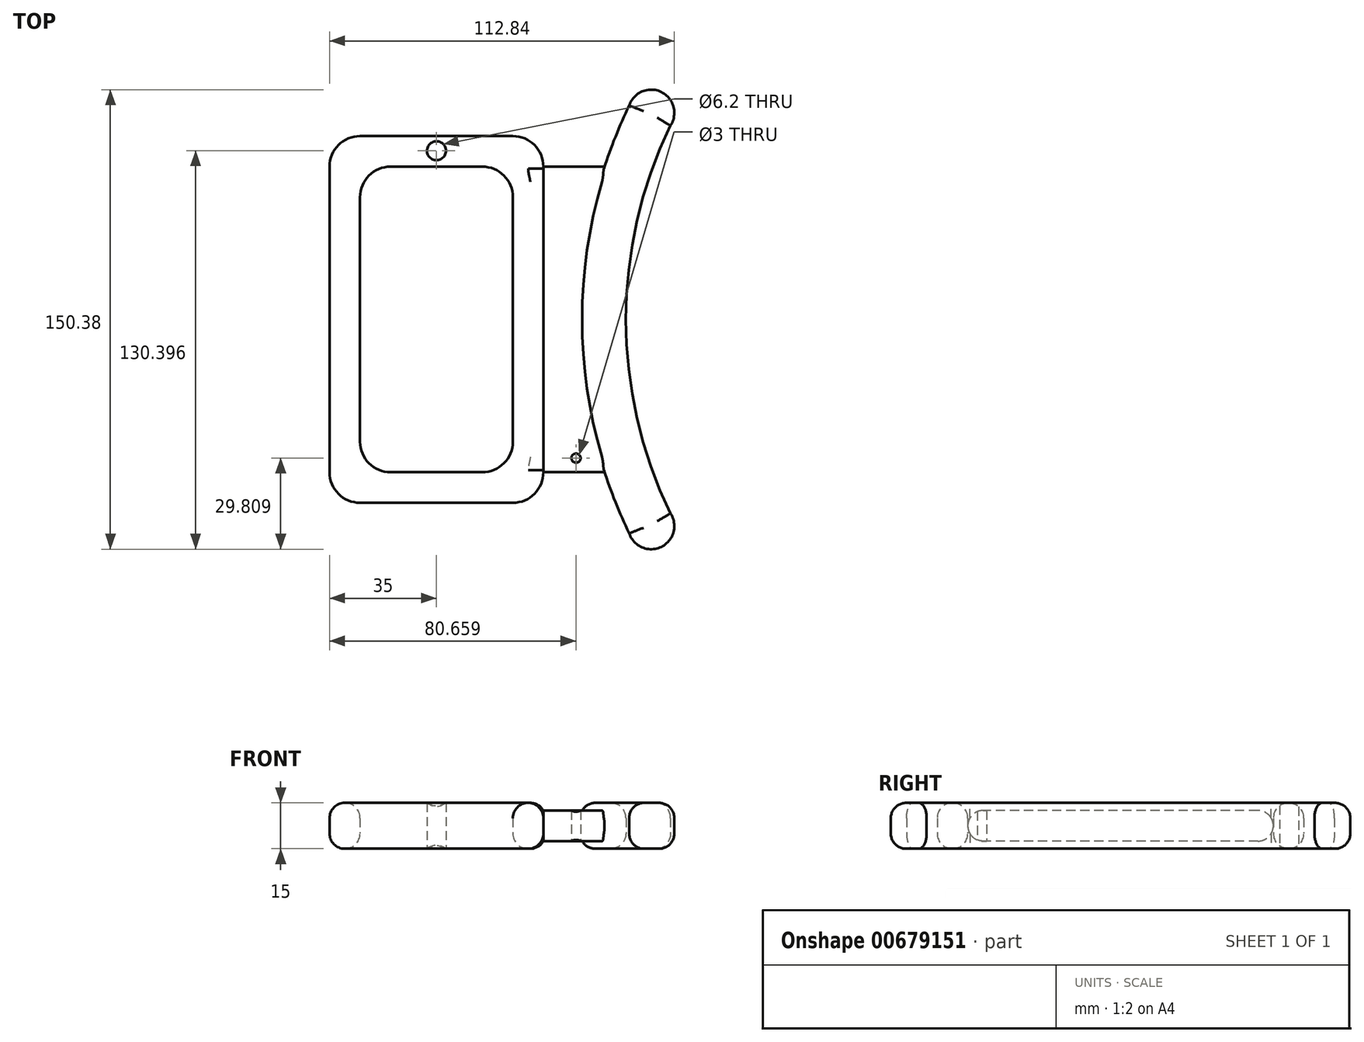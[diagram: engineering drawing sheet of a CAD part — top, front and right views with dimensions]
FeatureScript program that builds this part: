
annotation { "Feature Type Name" : "Feature", "Feature Type Description" : "" }
export const myFeature = defineFeature(function(context is Context, id is Id, definition is map)
    precondition{}
    {
        {
            var Q0;
            Q0=qCreatedBy(makeId("Top.planeOp"),FACE);
            var sketch = newSketch(context, id + "F0", { "sketchPlane" : qUnion([Q0])});
            skLineSegment(sketch, "E0.bottom", {"start": v(15, 50) * mm, "end": v(-15, 50) * mm});
            skLineSegment(sketch, "E0.top", {"start": v(15, -50) * mm, "end": v(-15, -50) * mm});
            skLineSegment(sketch, "E0.left", {"start": v(25, 40) * mm, "end": v(25, -40) * mm});
            skLineSegment(sketch, "E0.right", {"start": v(-25, 40) * mm, "end": v(-25, -40) * mm});
            skPoint(sketch, "E0.middle", {"position": v(0, 0) * mm});
            skLineSegment(sketch, "E1.0", {"start": v(35, 50) * mm, "end": v(35, -50) * mm});
            skLineSegment(sketch, "E1.1", {"start": v(25, 60) * mm, "end": v(-25, 60) * mm});
            skLineSegment(sketch, "E1.2", {"start": v(-35, 50) * mm, "end": v(-35, -50) * mm});
            skLineSegment(sketch, "E1.3", {"start": v(25, -60) * mm, "end": v(-25, -60) * mm});
            skLineSegment(sketch, "E2", {"start": v(35, -50) * mm, "end": v(55, -50) * mm});
            skLineSegment(sketch, "E3", {"start": v(0, 0) * mm, "end": v(75.3, 0) * mm, "construction": true});
            skLineSegment(sketch, "E4.MirrorCS", {"start": v(35, 50) * mm, "end": v(55, 50) * mm});
            skArc(sketch, "E5", {"start": v(63.1, 70) * mm, "mid": v(47, 0) * mm, "end": v(63.1, -70) * mm});
            skLineSegment(sketch, "E6.0", {"start": v(0, -70) * mm, "end": v(75.3, -70) * mm, "construction": true});
            skArc(sketch, "E7.0", {"start": v(76.59, 63.45) * mm, "mid": v(62, 0) * mm, "end": v(76.59, -63.45) * mm});
            skArc(sketch, "E8", {"start": v(76.59, 63.45) * mm, "mid": v(73.58, 74.43) * mm, "end": v(63.1, 70) * mm});
            skArc(sketch, "E9.MirrorCS", {"start": v(76.59, -63.45) * mm, "mid": v(73.58, -74.43) * mm, "end": v(63.1, -70) * mm});
            skPoint(sketch, "E10.visualSharp", {"position": v(-35, 60) * mm});
            skArc(sketch, "E10.filletArc", {"start": v(-25, 60) * mm, "mid": v(-32.07, 57.07) * mm, "end": v(-35, 50) * mm});
            skPoint(sketch, "E11.visualSharp", {"position": v(-35, -60) * mm});
            skArc(sketch, "E11.filletArc", {"start": v(-35, -50) * mm, "mid": v(-32.07, -57.07) * mm, "end": v(-25, -60) * mm});
            skPoint(sketch, "E12.visualSharp", {"position": v(35, 60) * mm});
            skArc(sketch, "E12.filletArc", {"start": v(35, 50) * mm, "mid": v(32.07, 57.07) * mm, "end": v(25, 60) * mm});
            skPoint(sketch, "E13.visualSharp", {"position": v(35, -60) * mm});
            skArc(sketch, "E13.filletArc", {"start": v(25, -60) * mm, "mid": v(32.07, -57.07) * mm, "end": v(35, -50) * mm});
            skArc(sketch, "E14.filletArc", {"start": v(25, 40) * mm, "mid": v(22.07, 47.07) * mm, "end": v(15, 50) * mm});
            skArc(sketch, "E15.filletArc", {"start": v(-15, 50) * mm, "mid": v(-22.07, 47.07) * mm, "end": v(-25, 40) * mm});
            skArc(sketch, "E16.filletArc", {"start": v(-25, -40) * mm, "mid": v(-22.07, -47.07) * mm, "end": v(-15, -50) * mm});
            skArc(sketch, "E17.filletArc", {"start": v(15, -50) * mm, "mid": v(22.07, -47.07) * mm, "end": v(25, -40) * mm});
            skCircle(sketch, "E18", {"center": v(0, 55.2) * mm, "radius": 3.1 * mm});
            skCircle(sketch, "E19", {"center": v(45.66, -45.38) * mm, "radius": 1.5 * mm});
            skSolve(sketch);
        }
        {
            var Q0;
            Q0=makeQuery(id+"F0.imprint","IMPRINT",FACE,{"disambiguationData":[TD([[makeQuery(id+"F0.imprint","IMPRINT",EDGE,{"derivedFrom":sQuery(id+"F0.wireOp",EDGE,"E0.bottom")}),-1.0]])]});
            extrude(context, id + "F1", {"entities" : qUnion([Q0]), "endBound" : BoundingType.SYMMETRIC, "depth" : 15 * mm, "offsetDistance" : 25 * mm});
        }
        {
            var Q0;
            Q0=makeQuery(id+"F0.imprint","IMPRINT",FACE,{"disambiguationData":[TD([[makeQuery(id+"F0.imprint","IMPRINT",EDGE,{"derivedFrom":sQuery(id+"F0.wireOp",EDGE,"E1.0")}),1.0]])]});
            extrude(context, id + "F2", {"entities" : qUnion([Q0]), "operationType" : NewBodyOperationType.ADD, "endBound" : BoundingType.SYMMETRIC, "depth" : 10 * mm, "offsetDistance" : 25 * mm});
        }
        {
            var Q0;
            Q0=makeQuery(id+"F0.imprint","IMPRINT",FACE,{"disambiguationData":[TD([[makeQuery(id+"F0.imprint","IMPRINT",EDGE,{"derivedFrom":sQuery(id+"F0.wireOp",EDGE,"E7.0")}),-1.0]])]});
            extrude(context, id + "F3", {"entities" : qUnion([Q0]), "operationType" : NewBodyOperationType.ADD, "endBound" : BoundingType.SYMMETRIC, "depth" : 15 * mm, "offsetDistance" : 25 * mm});
        }
        {
            var Q0;
            Q0=makeQuery(id+"F1.opExtrude","CAP_EDGE",EDGE,{"disambiguationData":[OSD([sQuery(id+"F0.wireOp",EDGE,"E0.left")])],"isStart":true});
            fillet(context, id + "F4", {"entities" : qUnion([Q0]), "radius" : 5 * mm, "tangentPropagation" : true, "allowEdgeOverflow" : false});
        }
        {
            var Q0;
            Q0=makeQuery(id+"F1.opExtrude","CAP_EDGE",EDGE,{"disambiguationData":[OSD([sQuery(id+"F0.wireOp",EDGE,"E0.right")])],"isStart":false});
            fillet(context, id + "F5", {"entities" : qUnion([Q0]), "radius" : 5 * mm, "tangentPropagation" : true, "allowEdgeOverflow" : false});
        }
        {
            var Q0;
            Q0=makeQuery(id+"F3.opExtrude","CAP_EDGE",EDGE,{"disambiguationData":[OSD([sQuery(id+"F0.wireOp",EDGE,"E5")])],"isStart":true});
            var Q1;
            Q1=makeQuery(id+"F3.opExtrude","CAP_EDGE",EDGE,{"disambiguationData":[OSD([sQuery(id+"F0.wireOp",EDGE,"E5")])],"isStart":false});
            var Q2;
            Q2=makeQuery(id+"F3.opExtrude","CAP_EDGE",EDGE,{"disambiguationData":[OSD([sQuery(id+"F0.wireOp",EDGE,"E7.0")])],"isStart":false});
            var Q3;
            Q3=makeQuery(id+"F3.opExtrude","CAP_EDGE",EDGE,{"disambiguationData":[OSD([sQuery(id+"F0.wireOp",EDGE,"E7.0")])],"isStart":true});
            var Q4;
            Q4=makeQuery(id+"F3.opExtrude","CAP_EDGE",EDGE,{"disambiguationData":[OSD([sQuery(id+"F0.wireOp",EDGE,"E8")])],"isStart":false});
            var Q5;
            Q5=makeQuery(id+"F3.opExtrude","CAP_EDGE",EDGE,{"disambiguationData":[OSD([sQuery(id+"F0.wireOp",EDGE,"E9.MirrorCS")])],"isStart":false});
            var Q6;
            Q6=makeQuery(id+"F3.opExtrude","CAP_EDGE",EDGE,{"disambiguationData":[OSD([sQuery(id+"F0.wireOp",EDGE,"E8")])],"isStart":true});
            var Q7;
            Q7=makeQuery(id+"F3.opExtrude","CAP_EDGE",EDGE,{"disambiguationData":[OSD([sQuery(id+"F0.wireOp",EDGE,"E9.MirrorCS")])],"isStart":true});
            fillet(context, id + "F6", {"entities" : qUnion([Q0, Q1, Q2, Q3, Q4, Q5, Q6, Q7]), "radius" : 5 * mm, "tangentPropagation" : true, "allowEdgeOverflow" : false});
        }
        {
            var Q0;
            Q0=makeQuery(id+"F2.opExtrude","CAP_EDGE",EDGE,{"disambiguationData":[OSD([sQuery(id+"F0.wireOp",EDGE,"E4.MirrorCS")])],"isStart":true});
            var Q1;
            Q1=makeQuery(id+"F2.opExtrude","CAP_EDGE",EDGE,{"disambiguationData":[OSD([sQuery(id+"F0.wireOp",EDGE,"E2")])],"isStart":true});
            var Q2;
            Q2=makeQuery(id+"F2.opExtrude","CAP_EDGE",EDGE,{"disambiguationData":[OSD([sQuery(id+"F0.wireOp",EDGE,"E2")])],"isStart":false});
            var Q3;
            Q3=makeQuery(id+"F2.opExtrude","CAP_EDGE",EDGE,{"disambiguationData":[OSD([sQuery(id+"F0.wireOp",EDGE,"E4.MirrorCS")])],"isStart":false});
            fillet(context, id + "F7", {"entities" : qUnion([Q0, Q1, Q2, Q3]), "radius" : 5 * mm, "tangentPropagation" : true, "allowEdgeOverflow" : false});
        }
        {
            var Q0;
            Q0=makeQuery(id+"F1.opExtrude","CAP_EDGE",EDGE,{"disambiguationData":[OSD([sQuery(id+"F0.wireOp",EDGE,"E1.2")])],"isStart":true});
            var Q1;
            Q1=makeQuery(id+"F1.opExtrude","CAP_EDGE",EDGE,{"disambiguationData":[OSD([sQuery(id+"F0.wireOp",EDGE,"E1.2")])],"isStart":false});
            fillet(context, id + "F8", {"entities" : qUnion([Q0, Q1]), "radius" : 5 * mm, "tangentPropagation" : true, "allowEdgeOverflow" : false});
        }
    });
